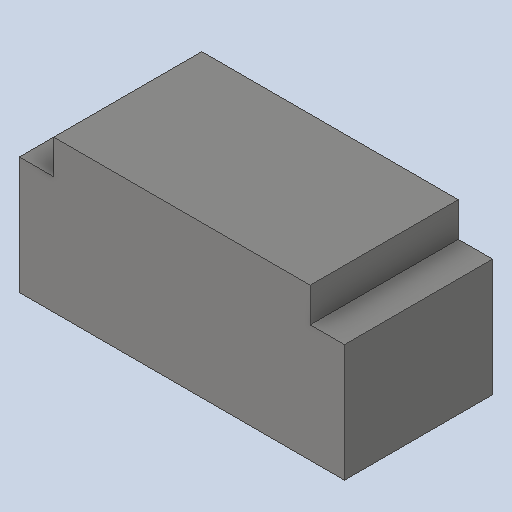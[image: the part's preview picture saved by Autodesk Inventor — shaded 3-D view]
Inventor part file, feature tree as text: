
AUTODESK INVENTOR PART (.ipt)
format: ipt  version: 2023 (Build 270158000, 158)  size: 109,056 bytes
history: native  units: mm
features: other x7, extrude x1, sketch x1
ambient origin geometry x8: Origin, YZ Plane, XZ Plane, XY Plane, X Axis, Y Axis, Z Axis, Center Point
bodies: Solid1 (feature_tree)
feature tree (9):
  extrude  "Extrusion1"  TaperAngle=0.0deg  [1 undecoded]
  other  "p1_XY"
  other  "p1_YZ"
  other  "p1_ZX"
  other  "p1_X"
  other  "p1_Y"
  other  "p1_Z"
  other  "p1_Center"
  sketch  "Sketch_1"  dims[d0=8.2mm d1=0.0mm d2=0.0mm]
note: 1 required parameter value undecoded (feature->parameter linkage not recoverable at this tier; creation-order binding heuristic only, values carry confidence <= 0.55)
